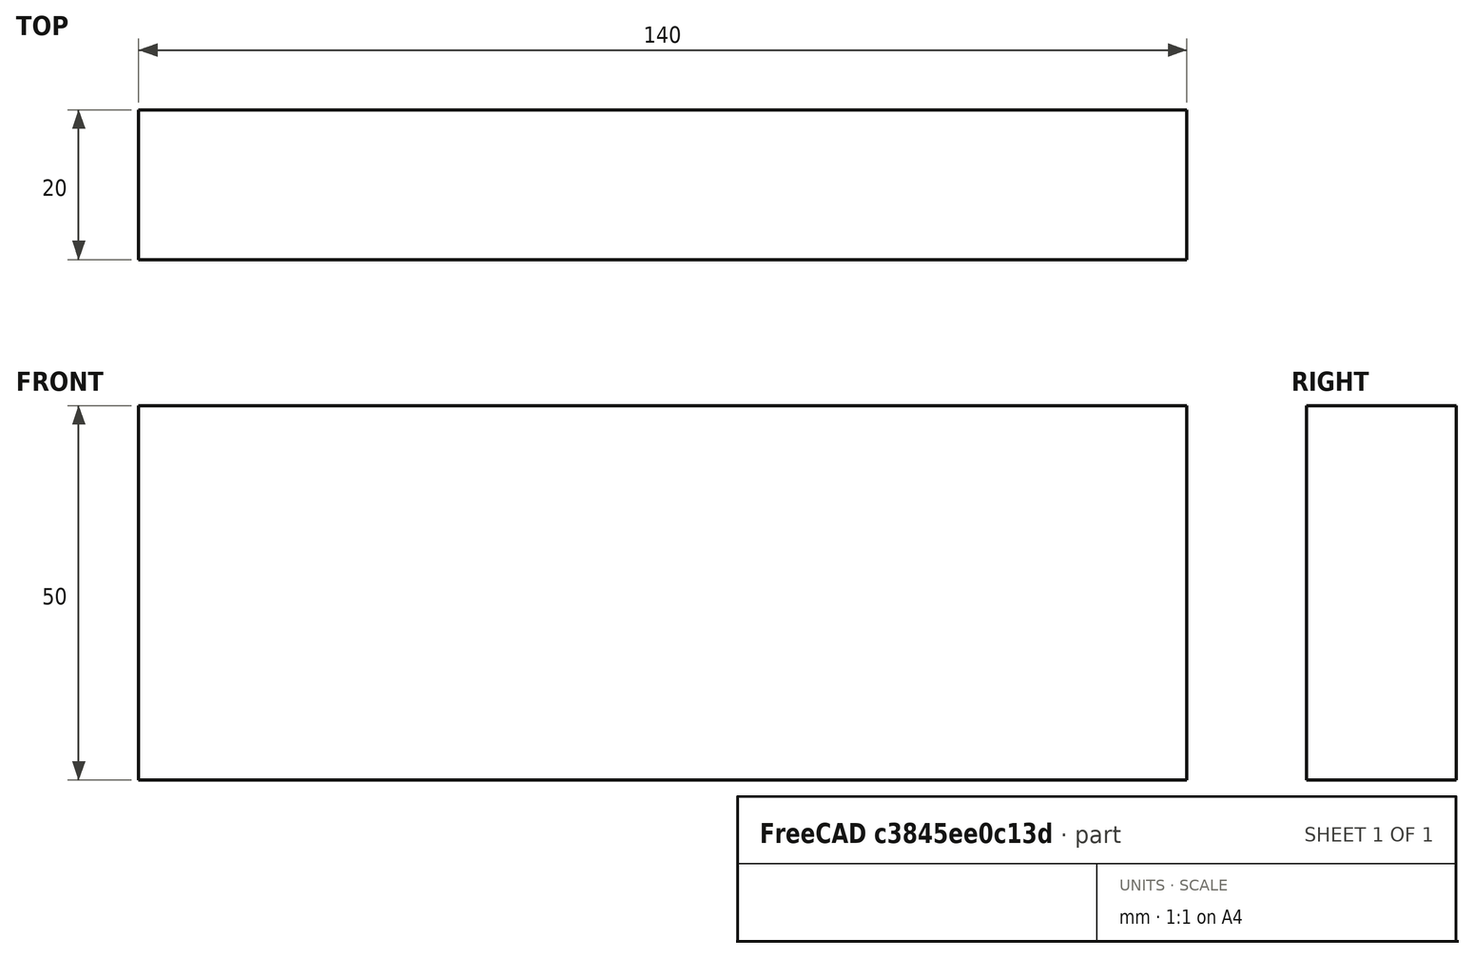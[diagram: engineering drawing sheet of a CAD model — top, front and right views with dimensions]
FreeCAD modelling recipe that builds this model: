
FCSTD DOCUMENT  (FreeCAD 0.15R4671 (Git))
Label: Flat Bar 140x20 EN10058 S235JR
License: All rights reserved
LicenseURL: http://en.wikipedia.org/wiki/All_rights_reserved
objects: Sketcher::SketchObject×1, Part::Extrusion×1
note: 2 computed .brp shape members not serialized (recipe doc carries the construction recipe); baked Part::Feature solids carry a one-line shape summary decoded from their .brp

FEATURE [Sketcher::SketchObject] Sketch
  sketch-geometry (4):
    g0: LineSegment StartX=-70 StartY=-10 StartZ=0 EndX=70 EndY=-10 EndZ=0
    g1: LineSegment StartX=70 StartY=-10 StartZ=0 EndX=70 EndY=10 EndZ=0
    g2: LineSegment StartX=70 StartY=10 StartZ=0 EndX=-70 EndY=10 EndZ=0
    g3: LineSegment StartX=-70 StartY=10 StartZ=0 EndX=-70 EndY=-10 EndZ=0
  constraints (12):
    c: Coincident(g0,g1)
    c: Coincident(g1,g2)
    c: Coincident(g2,g3)
    c: Coincident(g3,g0)
    c: Horizontal(g0)
    c: Horizontal(g2)
    c: Vertical(g1)
    c: Vertical(g3)
    c: Symmetric(g1,g2,g-2)
    c: Symmetric(g0,g1,g-1)
    c: DistanceY(g1) = 20
    c: DistanceX(g0) = 140
FEATURE [Part::Extrusion] Extrude  label="Flat Bar 140x20 EN10058 S235JR"
  Base = -> Sketch
  Dir = (0,0,50)
  Solid = true
